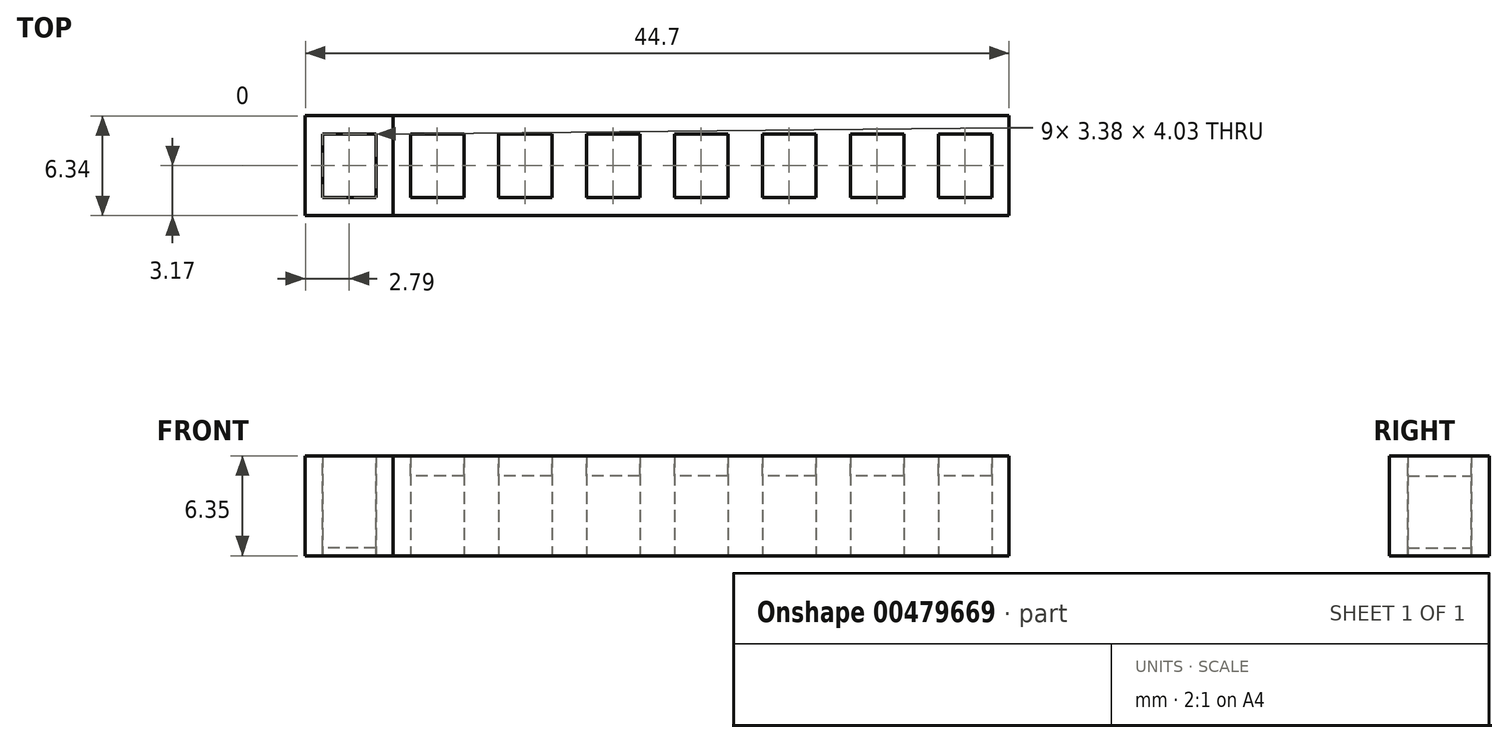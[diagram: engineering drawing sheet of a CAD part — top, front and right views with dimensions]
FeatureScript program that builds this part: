
annotation { "Feature Type Name" : "Feature", "Feature Type Description" : "" }
export const myFeature = defineFeature(function(context is Context, id is Id, definition is map)
    precondition{}
    {
        {
            var Q0;
            Q0=qCreatedBy(makeId("Top.planeOp"),FACE);
            var sketch = newSketch(context, id + "F0", { "sketchPlane" : qUnion([Q0])});
            skLineSegment(sketch, "E0.bottom", {"start": v(2.8, -3.17) * mm, "end": v(-2.8, -3.18) * mm});
            skLineSegment(sketch, "E0.top", {"start": v(2.8, 3.18) * mm, "end": v(-2.8, 3.18) * mm});
            skLineSegment(sketch, "E0.left", {"start": v(2.8, -3.17) * mm, "end": v(2.8, 3.18) * mm});
            skLineSegment(sketch, "E0.right", {"start": v(-2.8, -3.18) * mm, "end": v(-2.8, 3.18) * mm});
            skPoint(sketch, "E0.middle", {"position": v(0, 0) * mm});
            skLineSegment(sketch, "E1.bottom", {"start": v(1.7, -2.01) * mm, "end": v(-1.7, -2.01) * mm});
            skLineSegment(sketch, "E1.top", {"start": v(1.7, 2.01) * mm, "end": v(-1.7, 2.01) * mm});
            skLineSegment(sketch, "E1.left", {"start": v(1.7, -2.01) * mm, "end": v(1.7, 2.01) * mm});
            skLineSegment(sketch, "E1.right", {"start": v(-1.7, -2.01) * mm, "end": v(-1.7, 2.01) * mm});
            skLineSegment(sketch, "E2.bottom", {"start": v(8.38, -3.17) * mm, "end": v(2.8, -3.17) * mm});
            skLineSegment(sketch, "E2.top", {"start": v(8.38, 3.18) * mm, "end": v(2.8, 3.18) * mm});
            skLineSegment(sketch, "E2.left", {"start": v(8.38, -3.17) * mm, "end": v(8.38, 3.18) * mm});
            skPoint(sketch, "E2.middle", {"position": v(5.59, 0) * mm});
            skLineSegment(sketch, "E3.bottom", {"start": v(7.28, -2.01) * mm, "end": v(3.9, -2.01) * mm});
            skLineSegment(sketch, "E3.top", {"start": v(7.28, 2.01) * mm, "end": v(3.9, 2.01) * mm});
            skLineSegment(sketch, "E3.left", {"start": v(7.28, -2.01) * mm, "end": v(7.28, 2.01) * mm});
            skLineSegment(sketch, "E3.right", {"start": v(3.9, -2.01) * mm, "end": v(3.9, 2.01) * mm});
            skLineSegment(sketch, "E4.bottom", {"start": v(13.97, -3.17) * mm, "end": v(8.38, -3.17) * mm});
            skLineSegment(sketch, "E4.top", {"start": v(13.97, 3.18) * mm, "end": v(8.38, 3.18) * mm});
            skLineSegment(sketch, "E4.left", {"start": v(13.97, -3.17) * mm, "end": v(13.97, 3.18) * mm});
            skPoint(sketch, "E4.middle", {"position": v(11.18, 0) * mm});
            skLineSegment(sketch, "E5.bottom", {"start": v(12.87, -2.01) * mm, "end": v(9.48, -2.01) * mm});
            skLineSegment(sketch, "E5.top", {"start": v(12.87, 2.01) * mm, "end": v(9.48, 2.01) * mm});
            skLineSegment(sketch, "E5.left", {"start": v(12.87, -2.01) * mm, "end": v(12.87, 2.01) * mm});
            skLineSegment(sketch, "E5.right", {"start": v(9.48, -2.01) * mm, "end": v(9.48, 2.01) * mm});
            skLineSegment(sketch, "E6.bottom", {"start": v(19.56, -3.17) * mm, "end": v(13.97, -3.17) * mm});
            skLineSegment(sketch, "E6.top", {"start": v(19.56, 3.18) * mm, "end": v(13.97, 3.18) * mm});
            skLineSegment(sketch, "E6.left", {"start": v(19.56, -3.17) * mm, "end": v(19.56, 3.18) * mm});
            skPoint(sketch, "E6.middle", {"position": v(16.76, 0) * mm});
            skLineSegment(sketch, "E7.bottom", {"start": v(18.46, -2.01) * mm, "end": v(15.07, -2.01) * mm});
            skLineSegment(sketch, "E7.top", {"start": v(18.46, 2.01) * mm, "end": v(15.07, 2.01) * mm});
            skLineSegment(sketch, "E7.left", {"start": v(18.46, -2.01) * mm, "end": v(18.46, 2.01) * mm});
            skLineSegment(sketch, "E7.right", {"start": v(15.07, -2.01) * mm, "end": v(15.07, 2.01) * mm});
            skLineSegment(sketch, "E8.bottom", {"start": v(25.15, -3.17) * mm, "end": v(19.56, -3.17) * mm});
            skLineSegment(sketch, "E8.top", {"start": v(25.15, 3.18) * mm, "end": v(19.56, 3.18) * mm});
            skLineSegment(sketch, "E8.left", {"start": v(25.15, -3.17) * mm, "end": v(25.15, 3.18) * mm});
            skPoint(sketch, "E8.middle", {"position": v(22.35, 0) * mm});
            skLineSegment(sketch, "E9.bottom", {"start": v(24.04, -2.01) * mm, "end": v(20.66, -2.01) * mm});
            skLineSegment(sketch, "E9.top", {"start": v(24.04, 2.01) * mm, "end": v(20.66, 2.01) * mm});
            skLineSegment(sketch, "E9.left", {"start": v(24.04, -2.01) * mm, "end": v(24.04, 2.01) * mm});
            skLineSegment(sketch, "E9.right", {"start": v(20.66, -2.01) * mm, "end": v(20.66, 2.01) * mm});
            skLineSegment(sketch, "E10.bottom", {"start": v(30.73, -3.17) * mm, "end": v(25.15, -3.17) * mm});
            skLineSegment(sketch, "E10.top", {"start": v(30.73, 3.18) * mm, "end": v(25.15, 3.18) * mm});
            skLineSegment(sketch, "E10.left", {"start": v(30.73, -3.17) * mm, "end": v(30.73, 3.18) * mm});
            skPoint(sketch, "E10.middle", {"position": v(27.94, 0) * mm});
            skLineSegment(sketch, "E11.bottom", {"start": v(29.63, -2.01) * mm, "end": v(26.25, -2.01) * mm});
            skLineSegment(sketch, "E11.top", {"start": v(29.63, 2.01) * mm, "end": v(26.25, 2.01) * mm});
            skLineSegment(sketch, "E11.left", {"start": v(29.63, -2.01) * mm, "end": v(29.63, 2.01) * mm});
            skLineSegment(sketch, "E11.right", {"start": v(26.25, -2.01) * mm, "end": v(26.25, 2.01) * mm});
            skLineSegment(sketch, "E12.bottom", {"start": v(36.32, -3.17) * mm, "end": v(30.73, -3.17) * mm});
            skLineSegment(sketch, "E12.top", {"start": v(36.32, 3.18) * mm, "end": v(30.73, 3.18) * mm});
            skLineSegment(sketch, "E12.left", {"start": v(36.32, -3.17) * mm, "end": v(36.32, 3.18) * mm});
            skPoint(sketch, "E12.middle", {"position": v(33.53, 0) * mm});
            skLineSegment(sketch, "E13.bottom", {"start": v(35.22, -2.01) * mm, "end": v(31.84, -2.01) * mm});
            skLineSegment(sketch, "E13.top", {"start": v(35.22, 2.01) * mm, "end": v(31.84, 2.01) * mm});
            skLineSegment(sketch, "E13.left", {"start": v(35.22, -2.01) * mm, "end": v(35.22, 2.01) * mm});
            skLineSegment(sketch, "E13.right", {"start": v(31.84, -2.01) * mm, "end": v(31.84, 2.01) * mm});
            skLineSegment(sketch, "E14.bottom", {"start": v(41.91, -3.17) * mm, "end": v(36.32, -3.17) * mm});
            skLineSegment(sketch, "E14.top", {"start": v(41.91, 3.18) * mm, "end": v(36.32, 3.18) * mm});
            skLineSegment(sketch, "E14.left", {"start": v(41.91, -3.17) * mm, "end": v(41.91, 3.18) * mm});
            skPoint(sketch, "E14.middle", {"position": v(39.12, 0) * mm});
            skLineSegment(sketch, "E15.bottom", {"start": v(40.8, -2.01) * mm, "end": v(37.42, -2.01) * mm});
            skLineSegment(sketch, "E15.top", {"start": v(40.8, 2.01) * mm, "end": v(37.42, 2.01) * mm});
            skLineSegment(sketch, "E15.left", {"start": v(40.8, -2.01) * mm, "end": v(40.8, 2.01) * mm});
            skLineSegment(sketch, "E15.right", {"start": v(37.42, -2.01) * mm, "end": v(37.42, 2.01) * mm});
            skSolve(sketch);
        }
        {
            var Q0;
            Q0=makeQuery(id+"F0.imprint","IMPRINT",FACE,{"disambiguationData":[TD([[makeQuery(id+"F0.imprint","IMPRINT",EDGE,{"derivedFrom":sQuery(id+"F0.wireOp",EDGE,"E0.bottom")}),-1.0]])]});
            extrude(context, id + "F1", {"entities" : qUnion([Q0]), "depth" : 6.35 * mm});
        }
        {
            var Q0;
            Q0=makeQuery(id+"F1.opExtrude","CAP_FACE",FACE,{"disambiguationData":[OSD([sQuery(id+"F0.wireOp",EDGE,"E0.bottom"),sQuery(id+"F0.wireOp",EDGE,"E0.top"),sQuery(id+"F0.wireOp",EDGE,"E0.left"),sQuery(id+"F0.wireOp",EDGE,"E0.right"),sQuery(id+"F0.wireOp",EDGE,"E1.bottom"),sQuery(id+"F0.wireOp",EDGE,"E1.top"),sQuery(id+"F0.wireOp",EDGE,"E1.left"),sQuery(id+"F0.wireOp",EDGE,"E1.right")])],"isStart":false});
            var sketch = newSketch(context, id + "F2", { "sketchPlane" : qUnion([Q0])});
            skLineSegment(sketch, "E16.bottom", {"start": v(1.7, -2.01) * mm, "end": v(-1.7, -2.01) * mm});
            skLineSegment(sketch, "E16.top", {"start": v(1.7, 2.01) * mm, "end": v(-1.7, 2.01) * mm});
            skLineSegment(sketch, "E16.left", {"start": v(1.7, -2.01) * mm, "end": v(1.7, 2.01) * mm});
            skLineSegment(sketch, "E16.right", {"start": v(-1.7, -2.01) * mm, "end": v(-1.7, 2.01) * mm});
            skPoint(sketch, "E16.middle", {"position": v(0, 0) * mm});
            skSolve(sketch);
        }
        {
            var Q0;
            Q0=makeQuery(id+"F2.imprint","IMPRINT",FACE,{"disambiguationData":[TD([[makeQuery(id+"F2.imprint","IMPRINT",EDGE,{"derivedFrom":sQuery(id+"F2.wireOp",EDGE,"E16.bottom")}),-1.0]])]});
            extrude(context, id + "F3", {"entities" : qUnion([Q0]), "oppositeDirection" : true, "depth" : 5.84 * mm});
        }
        {
            var Q0;
            Q0=makeQuery(id+"F3.opExtrude","CAP_FACE",FACE,{"disambiguationData":[OSD([sQuery(id+"F2.wireOp",EDGE,"E16.bottom"),sQuery(id+"F2.wireOp",EDGE,"E16.top"),sQuery(id+"F2.wireOp",EDGE,"E16.left"),sQuery(id+"F2.wireOp",EDGE,"E16.right")])],"isStart":false});
            extrude(context, id + "F4", {"entities" : qUnion([Q0]), "depth" : 0.5 * mm});
        }
        {
            var Q0;
            Q0=qSketchRegion(id+"F0",true);
            extrude(context, id + "F5", {"entities" : qUnion([Q0]), "depth" : 6.35 * mm});
        }
        {
            var Q0;
            Q0=makeQuery(id+"F5.opExtrude","CAP_FACE",FACE,{"disambiguationData":[OSD([sQuery(id+"F0.wireOp",EDGE,"E0.bottom"),sQuery(id+"F0.wireOp",EDGE,"E0.top"),sQuery(id+"F0.wireOp",EDGE,"E0.right"),sQuery(id+"F0.wireOp",EDGE,"E1.bottom"),sQuery(id+"F0.wireOp",EDGE,"E1.top"),sQuery(id+"F0.wireOp",EDGE,"E1.left"),sQuery(id+"F0.wireOp",EDGE,"E1.right"),sQuery(id+"F0.wireOp",EDGE,"E2.bottom"),sQuery(id+"F0.wireOp",EDGE,"E2.top"),sQuery(id+"F0.wireOp",EDGE,"E3.bottom"),sQuery(id+"F0.wireOp",EDGE,"E3.top"),sQuery(id+"F0.wireOp",EDGE,"E3.left"),sQuery(id+"F0.wireOp",EDGE,"E3.right"),sQuery(id+"F0.wireOp",EDGE,"E4.bottom"),sQuery(id+"F0.wireOp",EDGE,"E4.top"),sQuery(id+"F0.wireOp",EDGE,"E5.bottom"),sQuery(id+"F0.wireOp",EDGE,"E5.top"),sQuery(id+"F0.wireOp",EDGE,"E5.left"),sQuery(id+"F0.wireOp",EDGE,"E5.right"),sQuery(id+"F0.wireOp",EDGE,"E6.bottom"),sQuery(id+"F0.wireOp",EDGE,"E6.top"),sQuery(id+"F0.wireOp",EDGE,"E7.bottom"),sQuery(id+"F0.wireOp",EDGE,"E7.top"),sQuery(id+"F0.wireOp",EDGE,"E7.left"),sQuery(id+"F0.wireOp",EDGE,"E7.right"),sQuery(id+"F0.wireOp",EDGE,"E8.bottom"),sQuery(id+"F0.wireOp",EDGE,"E8.top"),sQuery(id+"F0.wireOp",EDGE,"E9.bottom"),sQuery(id+"F0.wireOp",EDGE,"E9.top"),sQuery(id+"F0.wireOp",EDGE,"E9.left"),sQuery(id+"F0.wireOp",EDGE,"E9.right"),sQuery(id+"F0.wireOp",EDGE,"E10.bottom"),sQuery(id+"F0.wireOp",EDGE,"E10.top"),sQuery(id+"F0.wireOp",EDGE,"E11.bottom"),sQuery(id+"F0.wireOp",EDGE,"E11.top"),sQuery(id+"F0.wireOp",EDGE,"E11.left"),sQuery(id+"F0.wireOp",EDGE,"E11.right"),sQuery(id+"F0.wireOp",EDGE,"E12.bottom"),sQuery(id+"F0.wireOp",EDGE,"E12.top"),sQuery(id+"F0.wireOp",EDGE,"E13.bottom"),sQuery(id+"F0.wireOp",EDGE,"E13.top"),sQuery(id+"F0.wireOp",EDGE,"E13.left"),sQuery(id+"F0.wireOp",EDGE,"E13.right"),sQuery(id+"F0.wireOp",EDGE,"E14.bottom"),sQuery(id+"F0.wireOp",EDGE,"E14.top"),sQuery(id+"F0.wireOp",EDGE,"E14.left"),sQuery(id+"F0.wireOp",EDGE,"E15.bottom"),sQuery(id+"F0.wireOp",EDGE,"E15.top"),sQuery(id+"F0.wireOp",EDGE,"E15.left"),sQuery(id+"F0.wireOp",EDGE,"E15.right")])],"isStart":false});
            var sketch = newSketch(context, id + "F6", { "sketchPlane" : qUnion([Q0])});
            skLineSegment(sketch, "E17.bottom", {"start": v(3.9, 2.01) * mm, "end": v(7.28, 2.01) * mm});
            skLineSegment(sketch, "E17.top", {"start": v(3.9, -2.01) * mm, "end": v(7.28, -2.01) * mm});
            skLineSegment(sketch, "E17.left", {"start": v(3.9, 2.01) * mm, "end": v(3.9, -2.01) * mm});
            skLineSegment(sketch, "E17.right", {"start": v(7.28, 2.01) * mm, "end": v(7.28, -2.01) * mm});
            skLineSegment(sketch, "E18.bottom", {"start": v(9.48, 2.01) * mm, "end": v(12.87, 2.01) * mm});
            skLineSegment(sketch, "E18.top", {"start": v(9.48, -2.01) * mm, "end": v(12.87, -2.01) * mm});
            skLineSegment(sketch, "E18.left", {"start": v(9.48, 2.01) * mm, "end": v(9.48, -2.01) * mm});
            skLineSegment(sketch, "E18.right", {"start": v(12.87, 2.01) * mm, "end": v(12.87, -2.01) * mm});
            skLineSegment(sketch, "E19.bottom", {"start": v(15.07, 2.01) * mm, "end": v(18.46, 2.01) * mm});
            skLineSegment(sketch, "E19.top", {"start": v(15.07, -2.01) * mm, "end": v(18.46, -2.01) * mm});
            skLineSegment(sketch, "E19.left", {"start": v(15.07, 2.01) * mm, "end": v(15.07, -2.01) * mm});
            skLineSegment(sketch, "E19.right", {"start": v(18.46, 2.01) * mm, "end": v(18.46, -2.01) * mm});
            skLineSegment(sketch, "E20.bottom", {"start": v(20.66, 2.01) * mm, "end": v(24.04, 2.01) * mm});
            skLineSegment(sketch, "E20.top", {"start": v(20.66, -2.01) * mm, "end": v(24.04, -2.01) * mm});
            skLineSegment(sketch, "E20.left", {"start": v(20.66, 2.01) * mm, "end": v(20.66, -2.01) * mm});
            skLineSegment(sketch, "E20.right", {"start": v(24.04, 2.01) * mm, "end": v(24.04, -2.01) * mm});
            skLineSegment(sketch, "E21.bottom", {"start": v(26.25, 2.01) * mm, "end": v(29.63, 2.01) * mm});
            skLineSegment(sketch, "E21.top", {"start": v(26.25, -2.01) * mm, "end": v(29.63, -2.01) * mm});
            skLineSegment(sketch, "E21.left", {"start": v(26.25, 2.01) * mm, "end": v(26.25, -2.01) * mm});
            skLineSegment(sketch, "E21.right", {"start": v(29.63, 2.01) * mm, "end": v(29.63, -2.01) * mm});
            skLineSegment(sketch, "E22.bottom", {"start": v(31.84, 2.01) * mm, "end": v(35.22, 2.01) * mm});
            skLineSegment(sketch, "E22.top", {"start": v(31.84, -2.01) * mm, "end": v(35.22, -2.01) * mm});
            skLineSegment(sketch, "E22.left", {"start": v(31.84, 2.01) * mm, "end": v(31.84, -2.01) * mm});
            skLineSegment(sketch, "E22.right", {"start": v(35.22, 2.01) * mm, "end": v(35.22, -2.01) * mm});
            skLineSegment(sketch, "E23.bottom", {"start": v(37.42, 2.01) * mm, "end": v(40.8, 2.01) * mm});
            skLineSegment(sketch, "E23.top", {"start": v(37.42, -2.01) * mm, "end": v(40.8, -2.01) * mm});
            skLineSegment(sketch, "E23.left", {"start": v(37.42, 2.01) * mm, "end": v(37.42, -2.01) * mm});
            skLineSegment(sketch, "E23.right", {"start": v(40.8, 2.01) * mm, "end": v(40.8, -2.01) * mm});
            skSolve(sketch);
        }
        {
            var Q0;
            Q0=makeQuery(id+"F6.imprint","IMPRINT",FACE,{"disambiguationData":[TD([[makeQuery(id+"F6.imprint","IMPRINT",EDGE,{"derivedFrom":sQuery(id+"F6.wireOp",EDGE,"E17.bottom")}),1.0]])]});
            var Q1;
            Q1=makeQuery(id+"F6.imprint","IMPRINT",FACE,{"disambiguationData":[TD([[makeQuery(id+"F6.imprint","IMPRINT",EDGE,{"derivedFrom":sQuery(id+"F6.wireOp",EDGE,"E18.bottom")}),1.0]])]});
            var Q2;
            Q2=makeQuery(id+"F6.imprint","IMPRINT",FACE,{"disambiguationData":[TD([[makeQuery(id+"F6.imprint","IMPRINT",EDGE,{"derivedFrom":sQuery(id+"F6.wireOp",EDGE,"E19.bottom")}),1.0]])]});
            var Q3;
            Q3=makeQuery(id+"F6.imprint","IMPRINT",FACE,{"disambiguationData":[TD([[makeQuery(id+"F6.imprint","IMPRINT",EDGE,{"derivedFrom":sQuery(id+"F6.wireOp",EDGE,"E20.bottom")}),1.0]])]});
            var Q4;
            Q4=makeQuery(id+"F6.imprint","IMPRINT",FACE,{"disambiguationData":[TD([[makeQuery(id+"F6.imprint","IMPRINT",EDGE,{"derivedFrom":sQuery(id+"F6.wireOp",EDGE,"E21.bottom")}),1.0]])]});
            var Q5;
            Q5=makeQuery(id+"F6.imprint","IMPRINT",FACE,{"disambiguationData":[TD([[makeQuery(id+"F6.imprint","IMPRINT",EDGE,{"derivedFrom":sQuery(id+"F6.wireOp",EDGE,"E22.bottom")}),1.0]])]});
            var Q6;
            Q6=makeQuery(id+"F6.imprint","IMPRINT",FACE,{"disambiguationData":[TD([[makeQuery(id+"F6.imprint","IMPRINT",EDGE,{"derivedFrom":sQuery(id+"F6.wireOp",EDGE,"E23.bottom")}),1.0]])]});
            extrude(context, id + "F7", {"entities" : qUnion([Q0, Q1, Q2, Q3, Q4, Q5, Q6]), "oppositeDirection" : true, "depth" : 1.27 * mm});
        }
    });
